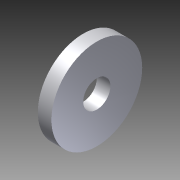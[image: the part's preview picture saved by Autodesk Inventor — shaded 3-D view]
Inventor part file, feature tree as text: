
AUTODESK INVENTOR PART (.ipt)
format: ipt  version: 2012 (Build 160160000, 160)  size: 602,112 bytes
history: native  units: in
note: dims shown in document units (in); Inventor stores cm internally (conversion verified against a paired STEP export)
features: extrude x3, sketch x1, imported_body x1
ambient origin geometry x8: Origin, YZ Plane, XZ Plane, XY Plane, X Axis, Y Axis, Z Axis, Center Point
feature tree (5):
  sketch  "Sketch1"  dims[d0=0.375in d3=0.3in d4=0.0in d5=1.0in d6=0.125in d7=0.125in d8=0.0625in d9=0.5625in d10=0.375in d11=0.0in d12=1.25in d13=1.0in d14=0.0in]
  extrude  "Extrusion2"  Depth=0.3in TaperAngle=0.0deg
  extrude  "Extrusion3"  Depth=1.0in
  extrude  "Extrusion4"  Depth=0.125in
  imported_body  "Base1"
